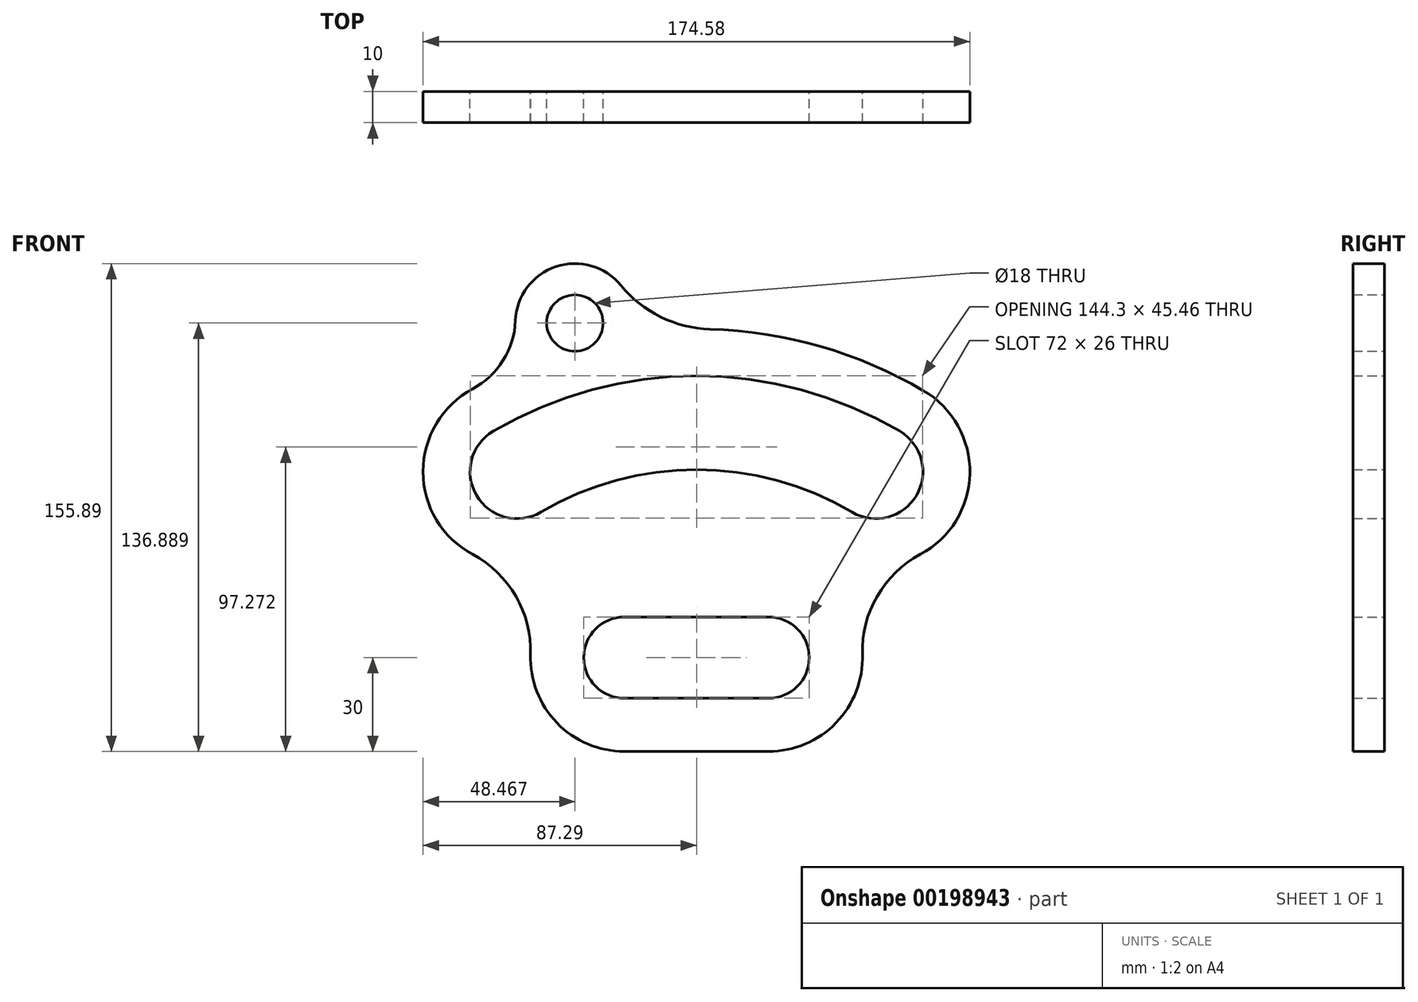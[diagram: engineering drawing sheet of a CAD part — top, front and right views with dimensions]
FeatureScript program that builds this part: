
annotation { "Feature Type Name" : "Feature", "Feature Type Description" : "" }
export const myFeature = defineFeature(function(context is Context, id is Id, definition is map)
    precondition{}
    {
        {
            var Q0;
            Q0=qCreatedBy(makeId("Front.planeOp"),FACE);
            var sketch = newSketch(context, id + "F0", { "sketchPlane" : qUnion([Q0])});
            skArc(sketch, "E0", {"start": v(-23, 13) * mm, "mid": v(-36, 0) * mm, "end": v(-23, -13) * mm});
            skArc(sketch, "E1", {"start": v(23, -13) * mm, "mid": v(36, 0) * mm, "end": v(23, 13) * mm});
            skLineSegment(sketch, "E2", {"start": v(-23, 13) * mm, "end": v(23, 13) * mm});
            skLineSegment(sketch, "E3", {"start": v(-23, -13) * mm, "end": v(23, -13) * mm});
            skArc(sketch, "E4", {"start": v(-23, -30) * mm, "mid": v(-44.55, -20.87) * mm, "end": v(-52.98, 0.96) * mm});
            skArc(sketch, "E5", {"start": v(23, -30) * mm, "mid": v(44.55, -20.87) * mm, "end": v(52.98, 0.96) * mm});
            skLineSegment(sketch, "E6", {"start": v(-23, -30) * mm, "end": v(23, -30) * mm});
            skArc(sketch, "E7", {"start": v(-57.3, 59.4) * mm, "mid": v(0, 75) * mm, "end": v(57.3, 59.4) * mm, "construction": true});
            skLineSegment(sketch, "E8", {"start": v(23, 0) * mm, "end": v(57.3, 59.4) * mm, "construction": true});
            skLineSegment(sketch, "E9", {"start": v(-57.3, 59.4) * mm, "end": v(-23, 0) * mm, "construction": true});
            skArc(sketch, "E10", {"start": v(-64.9, 72.33) * mm, "mid": v(-70.22, 51.8) * mm, "end": v(-49.69, 46.47) * mm});
            skArc(sketch, "E11", {"start": v(64.9, 72.33) * mm, "mid": v(70.22, 51.8) * mm, "end": v(49.69, 46.47) * mm});
            skArc(sketch, "E12", {"start": v(-64.9, 72.33) * mm, "mid": v(0, 90) * mm, "end": v(64.9, 72.33) * mm});
            skArc(sketch, "E13", {"start": v(-49.69, 46.47) * mm, "mid": v(0, 60) * mm, "end": v(49.69, 46.47) * mm});
            skArc(sketch, "E14", {"start": v(-71.49, 85.83) * mm, "mid": v(-87.3, 59.38) * mm, "end": v(-71.45, 32.95) * mm});
            skArc(sketch, "E15", {"start": v(71.45, 32.95) * mm, "mid": v(57.66, 19.6) * mm, "end": v(52.98, 0.96) * mm});
            skArc(sketch, "E16", {"start": v(-52.98, 0.96) * mm, "mid": v(-57.66, 19.6) * mm, "end": v(-71.45, 32.95) * mm});
            skLineSegment(sketch, "E17", {"start": v(0, -38) * mm, "end": v(-38.82, 106.89) * mm, "construction": true});
            skCircle(sketch, "E18", {"center": v(-38.82, 106.89) * mm, "radius": 9 * mm});
            skArc(sketch, "E19", {"start": v(-57.8, 107.67) * mm, "mid": v(-44.83, 124.91) * mm, "end": v(-24.1, 118.9) * mm});
            skArc(sketch, "E20.filletArc", {"start": v(-71.49, 85.83) * mm, "mid": v(-61.75, 94.94) * mm, "end": v(-57.8, 107.67) * mm});
            skPoint(sketch, "E21.visualSharp", {"position": v(-20.3, 102.65) * mm});
            skArc(sketch, "E21.filletArc", {"start": v(-24.1, 118.9) * mm, "mid": v(-11.46, 108.84) * mm, "end": v(4.22, 104.94) * mm});
            skArc(sketch, "E22", {"start": v(71.45, 32.95) * mm, "mid": v(87.29, 58.8) * mm, "end": v(72.5, 85.26) * mm});
            skArc(sketch, "E23", {"start": v(4.22, 104.94) * mm, "mid": v(39.6, 99.4) * mm, "end": v(72.5, 85.26) * mm});
            skSolve(sketch);
        }
        {
            var Q0;
            Q0=makeQuery(id+"F0.imprint","IMPRINT",FACE,{"disambiguationData":[TD([[makeQuery(id+"F0.imprint","IMPRINT",EDGE,{"derivedFrom":sQuery(id+"F0.wireOp",EDGE,"E0")}),-1.0]])]});
            extrude(context, id + "F1", {"entities" : qUnion([Q0]), "depth" : 10 * mm});
        }
    });
